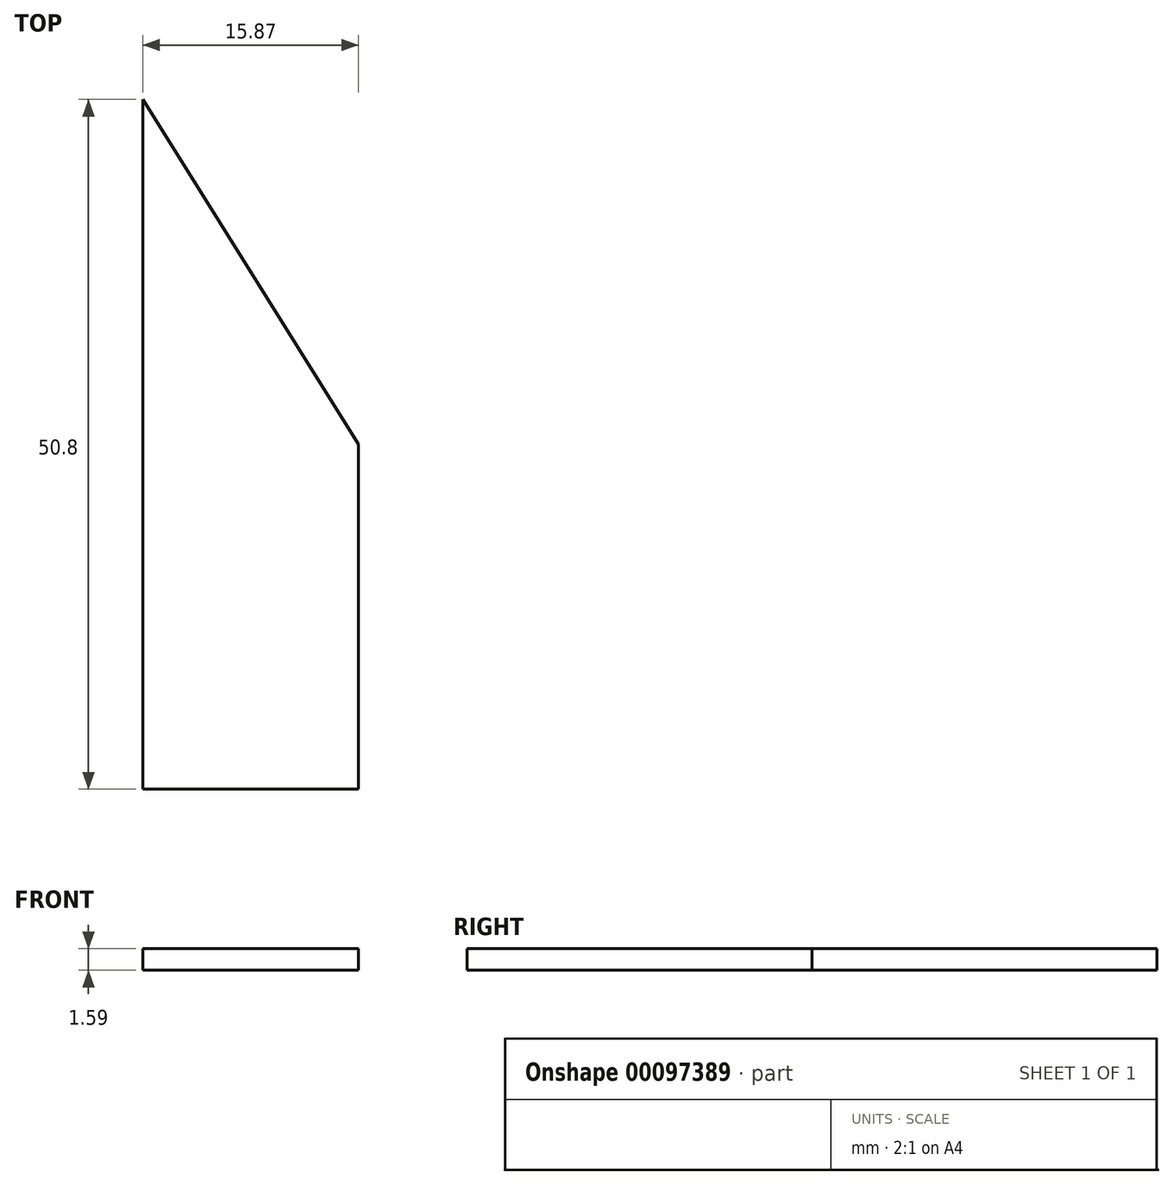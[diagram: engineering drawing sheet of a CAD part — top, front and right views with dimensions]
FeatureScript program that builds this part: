
annotation { "Feature Type Name" : "Feature", "Feature Type Description" : "" }
export const myFeature = defineFeature(function(context is Context, id is Id, definition is map)
    precondition{}
    {
        {
            var Q0;
            Q0=qCreatedBy(makeId("Top.planeOp"),FACE);
            var sketch = newSketch(context, id + "F0", { "sketchPlane" : qUnion([Q0])});
            skLineSegment(sketch, "E0", {"start": v(2.6, -23.55) * mm, "end": v(-13.27, -23.55) * mm});
            skLineSegment(sketch, "E1", {"start": v(-13.27, -23.55) * mm, "end": v(-13.27, 27.25) * mm});
            skLineSegment(sketch, "E2", {"start": v(-13.27, 27.25) * mm, "end": v(2.6, 1.85) * mm});
            skLineSegment(sketch, "E3", {"start": v(2.6, 1.85) * mm, "end": v(2.6, -23.55) * mm});
            skSolve(sketch);
        }
        {
            var Q0;
            Q0=makeQuery(id+"F0.imprint","IMPRINT",FACE,{"disambiguationData":[TD([[makeQuery(id+"F0.imprint","IMPRINT",EDGE,{"derivedFrom":sQuery(id+"F0.wireOp",EDGE,"E0")}),-1.0]])]});
            extrude(context, id + "F1", {"entities" : qUnion([Q0]), "depth" : 1.59 * mm});
        }
    });
